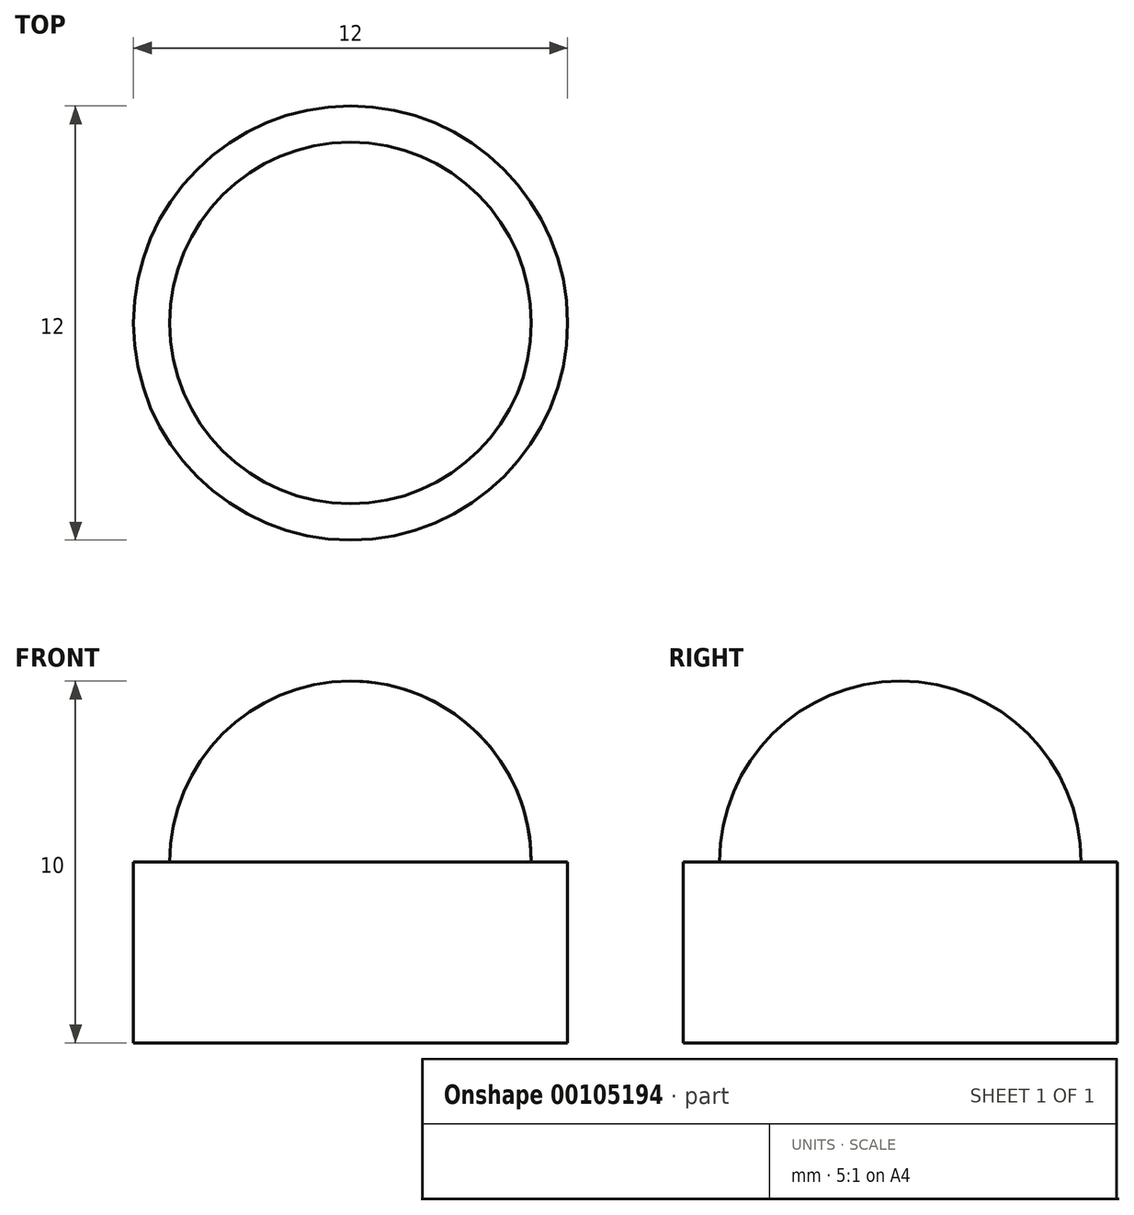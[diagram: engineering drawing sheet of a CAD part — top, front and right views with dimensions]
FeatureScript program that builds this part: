
annotation { "Feature Type Name" : "Feature", "Feature Type Description" : "" }
export const myFeature = defineFeature(function(context is Context, id is Id, definition is map)
    precondition{}
    {
        {
            var Q0;
            Q0=qCreatedBy(makeId("Top.planeOp"),FACE);
            var sketch = newSketch(context, id + "F0", { "sketchPlane" : qUnion([Q0])});
            skCircle(sketch, "E0", {"center": v(0, 0) * mm, "radius": 6 * mm});
            skSolve(sketch);
        }
        {
            var Q0;
            Q0=qSketchRegion(id+"F0",true);
            extrude(context, id + "F1", {"entities" : qUnion([Q0]), "depth" : 5 * mm});
        }
        {
            var Q0;
            Q0=makeQuery(id+"F1.opExtrude","CAP_FACE",FACE,{"disambiguationData":[OSD([sQuery(id+"F0.wireOp",EDGE,"E0")])],"isStart":false});
            var sketch = newSketch(context, id + "F2", { "sketchPlane" : qUnion([Q0])});
            skSolve(sketch);
        }
        {
            var Q0;
            Q0=makeQuery(id+"F2.imprint","IMPRINT",FACE,{"disambiguationData":[TD([[makeQuery(id+"F2.imprint","IMPRINT",EDGE,{"derivedFrom":makeQuery(id+"F1.opExtrude","CAP_EDGE",EDGE,{"disambiguationData":[OSD([sQuery(id+"F0.wireOp",EDGE,"E0")])],"isStart":false})}),1.0]])]});
            var sketch = newSketch(context, id + "F3", { "sketchPlane" : qUnion([Q0])});
            skCircle(sketch, "E1", {"center": v(0, 0) * mm, "radius": 5 * mm});
            skSolve(sketch);
        }
        {
            var Q0;
            Q0=qSketchRegion(id+"F3",true);
            extrude(context, id + "F4", {"entities" : qUnion([Q0]), "operationType" : NewBodyOperationType.ADD, "depth" : 5 * mm});
        }
        {
            var Q0;
            Q0=makeQuery(id+"F4.opExtrude","CAP_EDGE",EDGE,{"disambiguationData":[OSD([sQuery(id+"F3.wireOp",EDGE,"E1")])],"isStart":false});
            fillet(context, id + "F5", {"entities" : qUnion([Q0]), "radius" : 5 * mm, "tangentPropagation" : true, "allowEdgeOverflow" : false});
        }
    });
